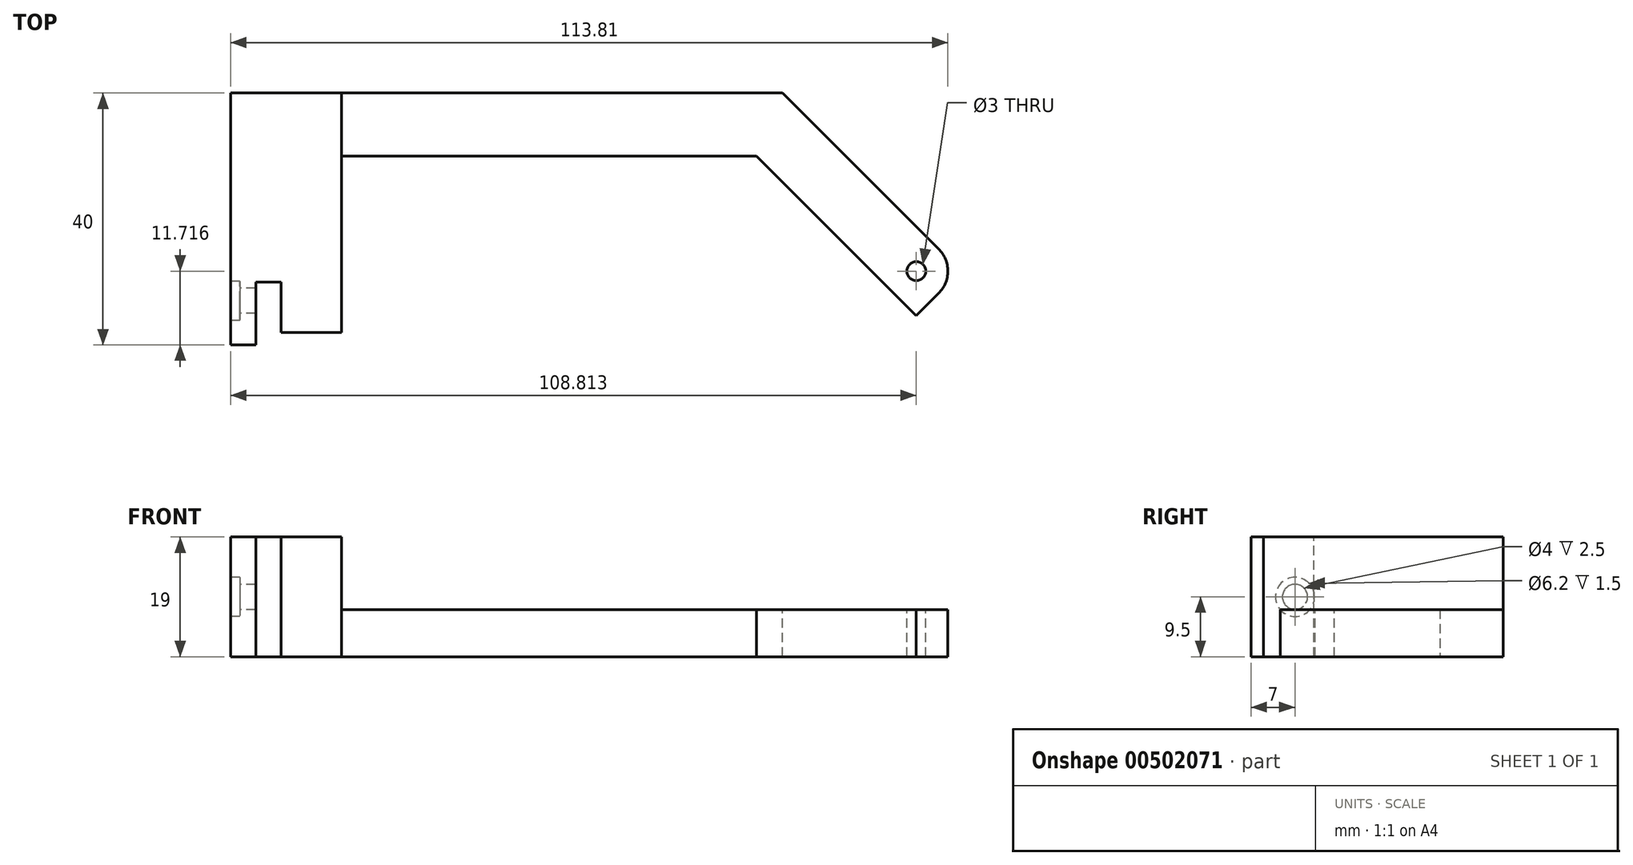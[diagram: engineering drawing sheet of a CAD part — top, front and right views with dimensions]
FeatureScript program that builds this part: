
annotation { "Feature Type Name" : "Feature", "Feature Type Description" : "" }
export const myFeature = defineFeature(function(context is Context, id is Id, definition is map)
    precondition{}
    {
        {
            var Q0;
            Q0=qCreatedBy(makeId("Front.planeOp"),FACE);
            var sketch = newSketch(context, id + "F0", { "sketchPlane" : qUnion([Q0])});
            skPoint(sketch, "E0.middle", {"position": v(0, 0) * mm});
            skLineSegment(sketch, "E1", {"start": v(-4.8, -9.5) * mm, "end": v(-4.8, 9.5) * mm});
            skLineSegment(sketch, "E2", {"start": v(-4.8, 9.5) * mm, "end": v(-1.8, 12.5) * mm});
            skLineSegment(sketch, "E3", {"start": v(-2.8, -15) * mm, "end": v(-4.8, -9.5) * mm});
            skLineSegment(sketch, "E4", {"start": v(0, -22.5) * mm, "end": v(0, 22.5) * mm, "construction": true});
            skLineSegment(sketch, "E5.MirrorCS", {"start": v(2.8, -15) * mm, "end": v(4.8, -9.5) * mm});
            skLineSegment(sketch, "E6.MirrorCS", {"start": v(4.8, 9.5) * mm, "end": v(1.8, 12.5) * mm});
            skLineSegment(sketch, "E7.MirrorCS", {"start": v(4.8, -9.5) * mm, "end": v(4.8, 9.5) * mm});
            skLineSegment(sketch, "E8", {"start": v(-1.8, 12.5) * mm, "end": v(1.8, 12.5) * mm});
            skLineSegment(sketch, "E9", {"start": v(-2.8, -15) * mm, "end": v(2.8, -15) * mm});
            skLineSegment(sketch, "E10", {"start": v(-4.8, 9.5) * mm, "end": v(4.8, 9.5) * mm});
            skLineSegment(sketch, "E11", {"start": v(-4.8, -9.5) * mm, "end": v(4.8, -9.5) * mm});
            skSolve(sketch);
        }
        {
            var Q0;
            Q0=makeQuery(id+"F0.imprint","IMPRINT",FACE,{"disambiguationData":[TD([[makeQuery(id+"F0.imprint","IMPRINT",EDGE,{"derivedFrom":sQuery(id+"F0.wireOp",EDGE,"E1")}),-1.0]])]});
            extrude(context, id + "F1", {"entities" : qUnion([Q0]), "depth" : 8 * mm});
        }
        {
            var Q0;
            Q0=makeQuery(id+"F1.opExtrude","CAP_FACE",FACE,{"disambiguationData":[OSD([sQuery(id+"F0.wireOp",EDGE,"E1"),sQuery(id+"F0.wireOp",EDGE,"E2"),sQuery(id+"F0.wireOp",EDGE,"E3"),sQuery(id+"F0.wireOp",EDGE,"E5.MirrorCS"),sQuery(id+"F0.wireOp",EDGE,"E6.MirrorCS"),sQuery(id+"F0.wireOp",EDGE,"E7.MirrorCS"),sQuery(id+"F0.wireOp",EDGE,"E8"),sQuery(id+"F0.wireOp",EDGE,"E9")])],"isStart":true});
            var sketch = newSketch(context, id + "F2", { "sketchPlane" : qUnion([Q0])});
            skLineSegment(sketch, "E12.bottom", {"start": v(4.8, 9.5) * mm, "end": v(8.8, 9.5) * mm});
            skLineSegment(sketch, "E12.top", {"start": v(4.8, -9.5) * mm, "end": v(8.8, -9.5) * mm});
            skLineSegment(sketch, "E12.left", {"start": v(4.8, 9.5) * mm, "end": v(4.8, -9.5) * mm});
            skLineSegment(sketch, "E12.right", {"start": v(8.8, 9.5) * mm, "end": v(8.8, -9.5) * mm});
            skLineSegment(sketch, "E13.bottom", {"start": v(-4.8, 9.5) * mm, "end": v(4.8, 9.5) * mm});
            skLineSegment(sketch, "E13.top", {"start": v(-4.8, -9.5) * mm, "end": v(4.8, -9.5) * mm});
            skLineSegment(sketch, "E13.left", {"start": v(-4.8, 9.5) * mm, "end": v(-4.8, -9.5) * mm});
            skLineSegment(sketch, "E14.bottom", {"start": v(8.8, 9.5) * mm, "end": v(12.8, 9.5) * mm});
            skLineSegment(sketch, "E14.top", {"start": v(8.8, -9.5) * mm, "end": v(12.8, -9.5) * mm});
            skLineSegment(sketch, "E14.right", {"start": v(12.8, 9.5) * mm, "end": v(12.8, -9.5) * mm});
            skSolve(sketch);
        }
        {
            var Q0;
            Q0=makeQuery(id+"F2.imprint","IMPRINT",FACE,{"disambiguationData":[TD([[makeQuery(id+"F2.imprint","IMPRINT",EDGE,{"derivedFrom":sQuery(id+"F2.wireOp",EDGE,"E12.bottom")}),-1.0]])]});
            var Q1;
            Q1=makeQuery(id+"F2.imprint","IMPRINT",FACE,{"disambiguationData":[TD([[makeQuery(id+"F2.imprint","IMPRINT",EDGE,{"derivedFrom":sQuery(id+"F2.wireOp",EDGE,"E13.bottom")}),-1.0]])]});
            var Q2;
            Q2=makeQuery(id+"F2.imprint","IMPRINT",FACE,{"disambiguationData":[TD([[makeQuery(id+"F2.imprint","IMPRINT",EDGE,{"derivedFrom":sQuery(id+"F2.wireOp",EDGE,"E14.bottom")}),-1.0]])]});
            var Q3;
            Q3=makeQuery(id+"F2.imprint","IMPRINT",FACE,{"disambiguationData":[TD([[makeQuery(id+"F2.imprint","IMPRINT",EDGE,{"derivedFrom":sQuery(id+"F2.wireOp",EDGE,"E13.bottom")}),1.0]])]});
            extrude(context, id + "F3", {"entities" : qUnion([Q0, Q1, Q2, Q3]), "operationType" : NewBodyOperationType.ADD, "depth" : 5 * mm});
        }
        {
            var Q0;
            Q0=makeQuery(id+"F3.opExtrude","CAP_FACE",FACE,{"disambiguationData":[OSD([sQuery(id+"F2.wireOp",EDGE,"E12.bottom"),sQuery(id+"F2.wireOp",EDGE,"E12.top"),sQuery(id+"F2.wireOp",EDGE,"E13.bottom"),sQuery(id+"F2.wireOp",EDGE,"E13.top"),sQuery(id+"F2.wireOp",EDGE,"E13.left"),sQuery(id+"F2.wireOp",EDGE,"E14.bottom"),sQuery(id+"F2.wireOp",EDGE,"E14.top"),sQuery(id+"F2.wireOp",EDGE,"E14.right")])],"isStart":true});
            var sketch = newSketch(context, id + "F4", { "sketchPlane" : qUnion([Q0])});
            skLineSegment(sketch, "E15.bottom", {"start": v(-12.8, 9.5) * mm, "end": v(-8.8, 9.5) * mm});
            skLineSegment(sketch, "E15.top", {"start": v(-12.8, -9.5) * mm, "end": v(-8.8, -9.5) * mm});
            skLineSegment(sketch, "E15.left", {"start": v(-12.8, 9.5) * mm, "end": v(-12.8, -9.5) * mm});
            skLineSegment(sketch, "E15.right", {"start": v(-8.8, 9.5) * mm, "end": v(-8.8, -9.5) * mm});
            skSolve(sketch);
        }
        {
            var Q0;
            Q0 = qSketchRegion(id + "F4", true);
            extrude(context, id + "F5", {"entities" : qUnion([Q0]), "operationType" : NewBodyOperationType.ADD, "depth" : 10 * mm});
        }
        {
            var Q0;
            Q0=makeQuery(id+"F5.boolean.opBoolean","MERGE",FACE,{"derivedFrom":[makeQuery(id+"F3.opExtrude","SWEPT_FACE",FACE,{"disambiguationData":[OSD([sQuery(id+"F2.wireOp",EDGE,"E14.right")])]}),makeQuery(id+"F5.opExtrude","SWEPT_FACE",FACE,{"disambiguationData":[OSD([sQuery(id+"F4.wireOp",EDGE,"E15.left")])]})]});
            var sketch = newSketch(context, id + "F6", { "sketchPlane" : qUnion([Q0])});
            skLineSegment(sketch, "E16", {"start": v(-5, 9.5) * mm, "end": v(0, 9.5) * mm, "construction": true});
            skLineSegment(sketch, "E17", {"start": v(0, 9.5) * mm, "end": v(0, -9.5) * mm, "construction": true});
            skLineSegment(sketch, "E18", {"start": v(0, 9.5) * mm, "end": v(6, 9.5) * mm, "construction": true});
            skPoint(sketch, "E19", {"position": v(6, 0) * mm});
            skCircle(sketch, "E20", {"center": v(3, 0) * mm, "radius": 2 * mm});
            skCircle(sketch, "E21", {"center": v(3, 0) * mm, "radius": 3.1 * mm});
            skLineSegment(sketch, "E22", {"start": v(6, 0) * mm, "end": v(3, 0) * mm, "construction": true});
            skSolve(sketch);
        }
        {
            var Q0;
            Q0=makeQuery(id+"F6.imprint","IMPRINT",FACE,{"disambiguationData":[TD([[makeQuery(id+"F6.imprint","IMPRINT",EDGE,{"derivedFrom":sQuery(id+"F6.wireOp",EDGE,"E20")}),1.0]])]});
            extrude(context, id + "F7", {"entities" : qUnion([Q0]), "operationType" : NewBodyOperationType.REMOVE, "endBound" : BoundingType.UP_TO_NEXT, "oppositeDirection" : true, "depth" : 7.1 * mm});
        }
        {
            var Q0;
            Q0=makeQuery(id+"F6.imprint","IMPRINT",FACE,{"disambiguationData":[TD([[makeQuery(id+"F6.imprint","IMPRINT",EDGE,{"derivedFrom":sQuery(id+"F6.wireOp",EDGE,"E20")}),-1.0]])]});
            extrude(context, id + "F8", {"entities" : qUnion([Q0]), "operationType" : NewBodyOperationType.REMOVE, "oppositeDirection" : true, "depth" : 1.5 * mm});
        }
        {
            var Q0;
            Q0=makeQuery(id+"F3.opExtrude","CAP_FACE",FACE,{"disambiguationData":[OSD([sQuery(id+"F2.wireOp",EDGE,"E12.bottom"),sQuery(id+"F2.wireOp",EDGE,"E12.top"),sQuery(id+"F2.wireOp",EDGE,"E13.bottom"),sQuery(id+"F2.wireOp",EDGE,"E13.top"),sQuery(id+"F2.wireOp",EDGE,"E13.left"),sQuery(id+"F2.wireOp",EDGE,"E14.bottom"),sQuery(id+"F2.wireOp",EDGE,"E14.top"),sQuery(id+"F2.wireOp",EDGE,"E14.right")])],"isStart":false});
            var sketch = newSketch(context, id + "F9", { "sketchPlane" : qUnion([Q0])});
            skLineSegment(sketch, "E23.bottom", {"start": v(12.8, -9.5) * mm, "end": v(-4.8, -9.5) * mm});
            skLineSegment(sketch, "E23.top", {"start": v(12.8, -2) * mm, "end": v(-4.8, -2) * mm});
            skLineSegment(sketch, "E23.left", {"start": v(12.8, -9.5) * mm, "end": v(12.8, -2) * mm});
            skLineSegment(sketch, "E23.right", {"start": v(-4.8, -9.5) * mm, "end": v(-4.8, -2) * mm});
            skSolve(sketch);
        }
        {
            var Q0;
            Q0 = qSketchRegion(id + "F9", true);
            extrude(context, id + "F10", {"entities" : qUnion([Q0]), "operationType" : NewBodyOperationType.ADD, "depth" : 25 * mm});
        }
        {
            var Q0;
            Q0=makeQuery(id+"F10.boolean.opBoolean","MERGE",FACE,{"derivedFrom":[makeQuery(id+"F3.boolean.opBoolean","MERGE",FACE,{"derivedFrom":[makeQuery(id+"F1.opExtrude","SWEPT_FACE",FACE,{"disambiguationData":[OSD([sQuery(id+"F0.wireOp",EDGE,"E7.MirrorCS")])]}),makeQuery(id+"F3.opExtrude","SWEPT_FACE",FACE,{"disambiguationData":[OSD([sQuery(id+"F2.wireOp",EDGE,"E13.left")])]})]}),makeQuery(id+"F10.opExtrude","SWEPT_FACE",FACE,{"disambiguationData":[OSD([sQuery(id+"F9.wireOp",EDGE,"E23.right")])]})]});
            var sketch = newSketch(context, id + "F11", { "sketchPlane" : qUnion([Q0])});
            skLineSegment(sketch, "E24.bottom", {"start": v(30, -2) * mm, "end": v(20, -2) * mm});
            skLineSegment(sketch, "E24.top", {"start": v(30, -9.5) * mm, "end": v(5, -9.5) * mm});
            skLineSegment(sketch, "E24.left", {"start": v(30, -2) * mm, "end": v(30, -9.5) * mm});
            skLineSegment(sketch, "E24.right", {"start": v(20, -2) * mm, "end": v(20, -9.5) * mm});
            skSolve(sketch);
        }
        {
            var Q0;
            Q0 = qSketchRegion(id + "F11", true);
            extrude(context, id + "F12", {"entities" : qUnion([Q0]), "operationType" : NewBodyOperationType.ADD, "depth" : 70 * mm});
        }
        {
            var Q0;
            Q0=makeQuery(id+"F12.boolean.opBoolean","MERGE",FACE,{"derivedFrom":[makeQuery(id+"F10.opExtrude","SWEPT_FACE",FACE,{"disambiguationData":[OSD([sQuery(id+"F9.wireOp",EDGE,"E23.top")])]}),makeQuery(id+"F12.opExtrude","SWEPT_FACE",FACE,{"disambiguationData":[OSD([sQuery(id+"F11.wireOp",EDGE,"E24.bottom")])]})]});
            var sketch = newSketch(context, id + "F13", { "sketchPlane" : qUnion([Q0])});
            skLineSegment(sketch, "E25", {"start": v(74.8, 20) * mm, "end": v(64.8, 20) * mm, "construction": true});
            skLineSegment(sketch, "E26", {"start": v(64.8, 20) * mm, "end": v(74.8, 30) * mm});
            skSolve(sketch);
        }
        {
            var Q0;
            {var subQ0=sQuery(id+"F13.wireOp",EDGE,"E26");Q0=makeQuery(id+"F13.imprint","IMPRINT",FACE,{"disambiguationData":[TD([[makeQuery(id+"F13.imprint","IMPRINT",EDGE,{"derivedFrom":subQ0}),-1.0]])]});}
            extrude(context, id + "F14", {"entities" : qUnion([Q0]), "operationType" : NewBodyOperationType.REMOVE, "oppositeDirection" : true, "depth" : 25 * mm});
        }
        {
            var Q0;
            Q0=makeQuery(id+"F14.boolean.opBoolean","COPY",FACE,{"derivedFrom":makeQuery(id+"F14.opExtrude","SWEPT_FACE",FACE,{"disambiguationData":[OSD([sQuery(id+"F13.wireOp",EDGE,"E26")])]})});
            extrude(context, id + "F15", {"entities" : qUnion([Q0]), "operationType" : NewBodyOperationType.ADD, "depth" : 40 * mm});
        }
        {
            var Q0;
            Q0=makeQuery(id+"F15.boolean.opBoolean","MERGE",FACE,{"derivedFrom":[makeQuery(id+"F12.boolean.opBoolean","MERGE",FACE,{"derivedFrom":[makeQuery(id+"F10.opExtrude","SWEPT_FACE",FACE,{"disambiguationData":[OSD([sQuery(id+"F9.wireOp",EDGE,"E23.top")])]}),makeQuery(id+"F12.opExtrude","SWEPT_FACE",FACE,{"disambiguationData":[OSD([sQuery(id+"F11.wireOp",EDGE,"E24.bottom")])]})]}),makeQuery(id+"F15.opExtrude","SWEPT_FACE",FACE,{"disambiguationData":[OSD([sQuery(id+"F13.wireOp",EDGE,"E26")])]})]});
            var sketch = newSketch(context, id + "F16", { "sketchPlane" : qUnion([Q0])});
            skLineSegment(sketch, "E27", {"start": v(99.55, -1.82) * mm, "end": v(96.01, 1.72) * mm, "construction": true});
            skCircle(sketch, "E28", {"center": v(96.01, 1.72) * mm, "radius": 1.5 * mm});
            skLineSegment(sketch, "E29", {"start": v(103.08, 1.72) * mm, "end": v(99.55, -1.82) * mm, "construction": true});
            skSolve(sketch);
        }
        {
            var Q0;
            Q0 = qSketchRegion(id + "F16", true);
            extrude(context, id + "F17", {"entities" : qUnion([Q0]), "operationType" : NewBodyOperationType.REMOVE, "oppositeDirection" : true, "depth" : 25 * mm});
        }
        {
            var Q0;
            Q0=makeQuery(id+"F3.opExtrude","CAP_FACE",FACE,{"disambiguationData":[OSD([sQuery(id+"F2.wireOp",EDGE,"E12.bottom"),sQuery(id+"F2.wireOp",EDGE,"E12.top"),sQuery(id+"F2.wireOp",EDGE,"E13.bottom"),sQuery(id+"F2.wireOp",EDGE,"E13.top"),sQuery(id+"F2.wireOp",EDGE,"E13.left"),sQuery(id+"F2.wireOp",EDGE,"E14.bottom"),sQuery(id+"F2.wireOp",EDGE,"E14.top"),sQuery(id+"F2.wireOp",EDGE,"E14.right")])],"isStart":false});
            extrude(context, id + "F18", {"entities" : qUnion([Q0]), "operationType" : NewBodyOperationType.ADD, "depth" : 25 * mm});
        }
        {
            var Q0;
            Q0=makeQuery(id+"F15.boolean.opBoolean","MERGE",FACE,{"derivedFrom":[makeQuery(id+"F12.boolean.opBoolean","MERGE",FACE,{"derivedFrom":[makeQuery(id+"F10.opExtrude","SWEPT_FACE",FACE,{"disambiguationData":[OSD([sQuery(id+"F9.wireOp",EDGE,"E23.top")])]}),makeQuery(id+"F12.opExtrude","SWEPT_FACE",FACE,{"disambiguationData":[OSD([sQuery(id+"F11.wireOp",EDGE,"E24.bottom")])]})]}),makeQuery(id+"F15.opExtrude","SWEPT_FACE",FACE,{"disambiguationData":[OSD([sQuery(id+"F13.wireOp",EDGE,"E26")])]})]});
            var sketch = newSketch(context, id + "F19", { "sketchPlane" : qUnion([Q0])});
            skLineSegment(sketch, "E30", {"start": v(103.08, 1.72) * mm, "end": v(96.01, -5.36) * mm, "construction": true});
            skLineSegment(sketch, "E31", {"start": v(96.01, -5.36) * mm, "end": v(70.66, 20) * mm});
            skLineSegment(sketch, "E32", {"start": v(70.66, 20) * mm, "end": v(64.8, 20) * mm});
            skSolve(sketch);
        }
        {
            var Q0;
            {var subQ0=sQuery(id+"F19.wireOp",EDGE,"E31");Q0=makeQuery(id+"F19.imprint","IMPRINT",FACE,{"disambiguationData":[TD([[makeQuery(id+"F19.imprint","IMPRINT",EDGE,{"derivedFrom":subQ0}),1.0]])]});}
            extrude(context, id + "F20", {"entities" : qUnion([Q0]), "operationType" : NewBodyOperationType.REMOVE, "oppositeDirection" : true, "depth" : 25 * mm});
        }
        {
            var Q0;
            Q0=makeQuery(id+"F20.boolean.opBoolean","COPY",EDGE,{"derivedFrom":makeQuery(id+"F20.opExtrude","SWEPT_EDGE",EDGE,{"disambiguationData":[OSD([sQuery(id+"F13.wireOp",EDGE,"E26"),sQuery(id+"F19.wireOp",EDGE,"E31")])]})});
            var Q1;
            Q1=makeQuery(id+"F15.opExtrude","CAP_EDGE",EDGE,{"disambiguationData":[OSD([sQuery(id+"F9.wireOp",EDGE,"E23.top"),sQuery(id+"F11.wireOp",EDGE,"E24.bottom"),sQuery(id+"F11.wireOp",EDGE,"E24.left"),sQuery(id+"F13.wireOp",EDGE,"E26")])],"isStart":false});
            fillet(context, id + "F21", {"entities" : qUnion([Q0, Q1]), "radius" : 5 * mm, "tangentPropagation" : true, "allowEdgeOverflow" : false});
        }
    });
